# Revit family: IS_Finesse_E3393_BIM_NL
name_source: partatom
category: Plumbing Fixtures
units: mm (PartAtom-declared; Revit-internal decimal feet)

## family parameters
Cut with Voids When Loaded = No
Host = Face
Maintain Annotation Orientation = No
OmniClass Number = 23.45.05.14.21.11
OmniClass Title = Bath/Shower Units
Part Type = Normal
Room Calculation Point = No
Round Connector Dimension = Use Diameter
Shared = Yes

## types (6) — shared parameters
Accessories = https://www.idealstandard.nl
Afmetingen = 1000 x 505 x 370mm
AfstandsEenheid = millimeter
AreaUnits = millimeters
Artikelomschrijving = FINESSE | Wastafelmeubel 1000x505x370 mm, 1 lade
Assembly Code = C1030200
AssetType = Fixed
Auteur = Ideal Standard
BIMObjectName = ISI_IdealStandard_Furniture_Finesse_E3393
BREEAM = No
Beschrijvinggarantie = Fabrieksgarantie
BimObjectNaam = ISI_IdealStandard_Furniture_Finesse_E3393
Brand = Ideal Standard
Breedte = 1000
ConnectionType = Plumbing
CurrencyUnit = €
Default Elevation = 1219 mm
Description = FINESSE | Basin unit 1000x505x370 mm, 1 drawer
Diepte = 504,999999999984
DurationUnit = year
DuurEenheid = jaar
ECA = No
EPD = https://www.idealstandard.nl
ExpectedLife = 30
Garantieunits = Jaar
GemaaktOp = 2024/09/04
Help = https://www.idealstandard.nl
Hoogte = 370
Hulp = https://www.idealstandard.nl
IfcExportAs = IfcFurnitureType
Installatieinstructies = https://www.idealstandard.nl
InstallationInstructions = https://www.idealstandard.nl
Lengte = 504,999999999984
LinearUnits = millimeters
Manufacturer = Ideal Standard
ManufacturerURL = https://www.idealstandard.nl
Materiaal = hout
Merk = Ideal Standard
ModelReference = FINESSE | Basin unit 1000x505x370 mm, 1 drawer
NBSDescription = Baths
Name = ISI_Furniture_Finesse_E3393_IdealStandard
NominalDepth = 505 mm  [stored 1.65682 ft]
NominalHeight = 370 mm  [stored 1.21391 ft]
NominalLength = 505 mm  [stored 1.65682 ft]
NominalWidth = 1000 mm  [stored 3.28084 ft]
ProductInformation = https://www.idealstandard.nl
ProductSoort = Meubilair
Productinformatie = https://www.idealstandard.nl
Shape = Rectangular
Size = 1000 x 505 x 370mm
Space = Internal
SpareParts = https://www.idealstandard.nl
TMV3 = No
Telefoonnummer = 077 355 08 08
Typeconnectie = Sanitair
URL = https://www.idealstandard.nl
Uniclass2015Code = Pr_40_20_76
Uniclass2015Title = Sanitary accessories
Uniclass2015Version = Products v1.34
Urlproducent = https://www.idealstandard.nl
ValutaEenheid = €
Versie = 1
Version = 1
VolumeUnits = Litres
Volumeunits = Liter
Vorm = Rechthoekig
WRAS = No
WarrantyDescription = Manufacturers Warranty
WarrantyDurationParts = 25
WarrantyDurationUnit = year
WarrantyGuarantorParts = https://www.idealstandard.nl
WaterEfficientProduct = No
Wisselstukken = https://www.idealstandard.nl
zero-valued in all types: Vervangingskosten

## per-type parameters (varying)
| type | Afwerking | Artikelnummer | Artikelreferentie | BarCode | Color | Eigenschappen | Features | Finish | Kleur | MAT | Model | ModelNumber | NettWeight | Nettogewicht |
| E3393UP - FINESSE VTY UN 1DRW 100X50CM GEMT | Greige mat | E3393UP | FINESSE / Wastafelmeubel 1000x505x370 mm in mat greige afwerking, 1 lade / Volledige extractielade, Softclose, Voorgemonteerd, Duurzaam geproduceerd hout | 5017830565536 | greige matt | FINESSE / Wastafelmeubel 1000x505x370 mm in mat greige afwerking, 1 lade / Volledige extractielade, Softclose, Voorgemonteerd, Duurzaam geproduceerd hout | FINESSE / Basin unit 1000x505x370 mm in greige matt finish, 1 drawer / Full extraction drawer, Soft close, Assembled, Sustainably sourced wood | greige matt | Greige mat | UP | E3393UP | E3393UP | 27.09 Kg | 27.09 Kg |
| E3393UQ - FINESSE VTY UN 1DRW 100X50CM ABMT | Mat asblauw | E3393UQ | FINESSE / Wastafelmeubel 1000x505x370 mm in matt ashblue afwerking, 1 lade / Volledige extractielade, Softclose, Voorgemonteerd, Duurzaam geproduceerd hout | 5017830565543 | matt ashblue | FINESSE / Wastafelmeubel 1000x505x370 mm in matt ashblue afwerking, 1 lade / Volledige extractielade, Softclose, Voorgemonteerd, Duurzaam geproduceerd hout | FINESSE / Basin unit 1000x505x370 mm in matt ashblue finish, 1 drawer / Full extraction drawer, Soft close, Assembled, Sustainably sourced wood | matt ashblue | Mat asblauw | UQ | E3393UQ | E3393UQ | 26.32 Kg | 26.32 Kg |
| E3393UR - FINESSE VTY UN 1DRW 100X50CM DKEM | Donkere iep | E3393UR | FINESSE / Wastafelmeubel 1000x505x370 mm in dark elm afwerking, 1 lade / Volledige extractielade, Softclose, Voorgemonteerd, Duurzaam geproduceerd hout | 5017830565550 | dark elm | FINESSE / Wastafelmeubel 1000x505x370 mm in dark elm afwerking, 1 lade / Volledige extractielade, Softclose, Voorgemonteerd, Duurzaam geproduceerd hout | FINESSE / Basin unit 1000x505x370 mm in dark elm finish, 1 drawer / Full extraction drawer, Soft close, Assembled, Sustainably sourced wood | dark elm | Donkere iep | UR | E3393UR | E3393UR | 25.37 Kg | 25.37 Kg |
| E3393US - FINESSE VTY UN 1DRW 100X50CM WOAK | Witte eik | E3393US | FINESSE / Wastafelmeubel 1000x505x370 mm in white oak afwerking, 1 lade / Volledige extractielade, Softclose, Voorgemonteerd, Duurzaam geproduceerd hout | 5017830565567 | white oak | FINESSE / Wastafelmeubel 1000x505x370 mm in white oak afwerking, 1 lade / Volledige extractielade, Softclose, Voorgemonteerd, Duurzaam geproduceerd hout | FINESSE / Basin unit 1000x505x370 mm in white oak finish, 1 drawer / Full extraction drawer, Soft close, Assembled, Sustainably sourced wood | white oak | Witte eik | US | E3393US | E3393US | 26.06 Kg | 26.06 Kg |
| E3393Y1 - FINESSE VTY UN 1DRW 100X50CM WHMT | Mat wit | E3393Y1 | FINESSE / Wastafelmeubel 1000x505x370 mm in matt white afwerking, 1 lade / Volledige extractielade, Softclose, Voorgemonteerd, Duurzaam geproduceerd hout | 5017830565574 | matt white | FINESSE / Wastafelmeubel 1000x505x370 mm in matt white afwerking, 1 lade / Volledige extractielade, Softclose, Voorgemonteerd, Duurzaam geproduceerd hout | FINESSE / Basin unit 1000x505x370 mm in matt white finish, 1 drawer / Full extraction drawer, Soft close, Assembled, Sustainably sourced wood | matt white | Mat wit | Y1 | E3393Y1 | E3393Y1 | 27.09 Kg | 27.09 Kg |
| E3393Y2 - FINESSE VTY UN 1DRW 100X50CM ANMT | Mat antraciet | E3393Y2 | FINESSE / Wastafelmeubel 1000x505x370 mm in matt anthracite afwerking, 1 lade / Volledige extractielade, Softclose, Voorgemonteerd, Duurzaam geproduceerd hout | 5017830565581 | matt anthracite | FINESSE / Wastafelmeubel 1000x505x370 mm in matt anthracite afwerking, 1 lade / Volledige extractielade, Softclose, Voorgemonteerd, Duurzaam geproduceerd hout | FINESSE / Basin unit 1000x505x370 mm in matt anthracite finish, 1 drawer / Full extraction drawer, Soft close, Assembled, Sustainably sourced wood | matt anthracite | Mat antraciet | Y2 | E3393Y2 | E3393Y2 | 27.09 Kg | 27.09 Kg |

note: [stored X ft] marks values corroborated as IEEE doubles in the binary element streams (Revit-internal decimal feet)

## geometry (parser evidence)
native form markers: Sweep x3
no freeform markers — native parametric forms only
